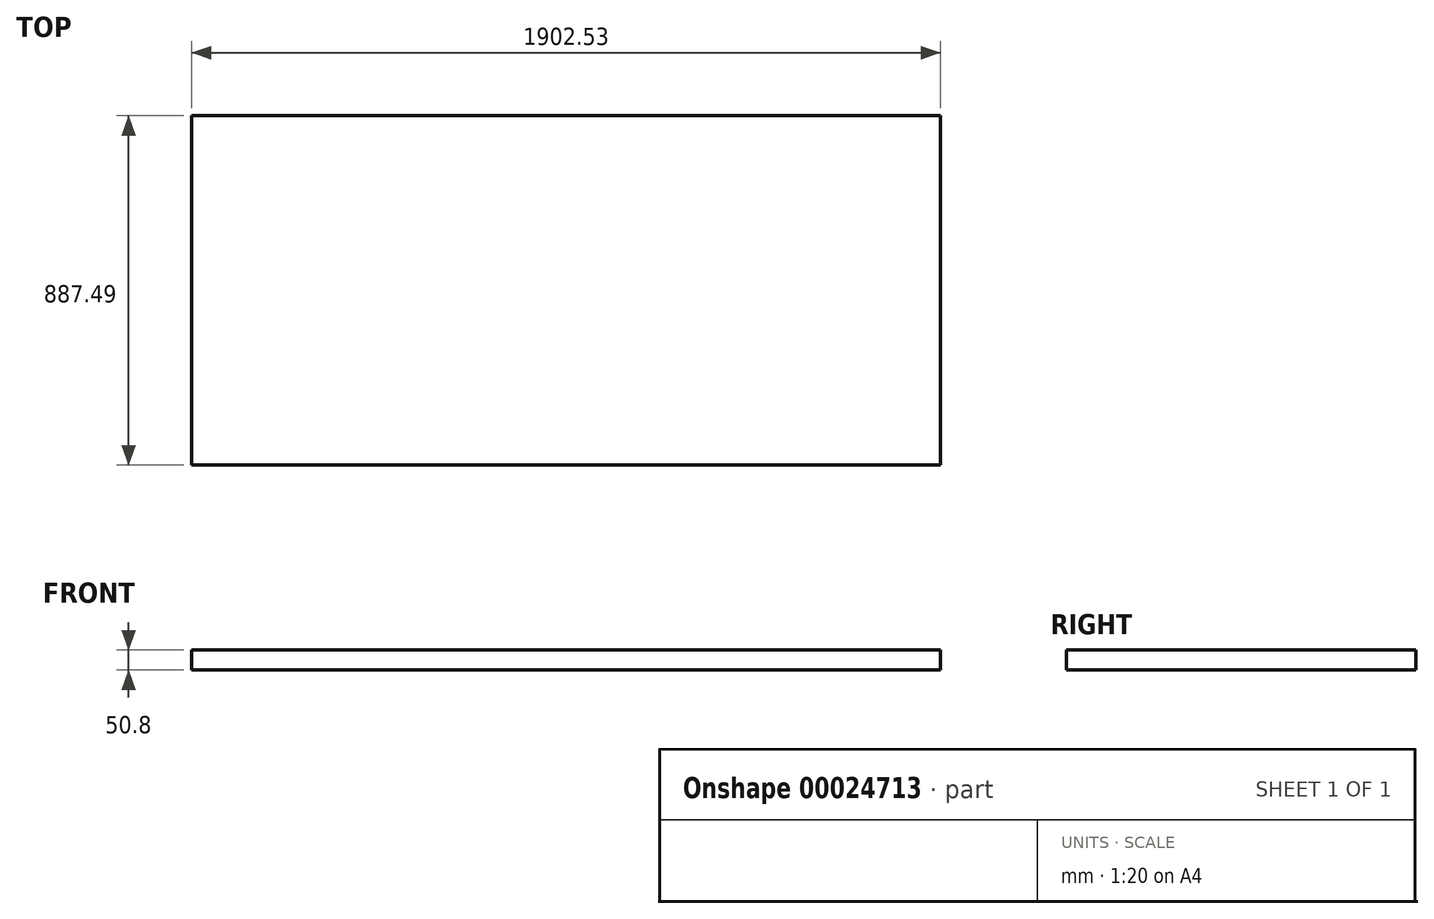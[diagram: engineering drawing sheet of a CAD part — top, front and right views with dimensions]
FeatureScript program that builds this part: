
annotation { "Feature Type Name" : "Feature", "Feature Type Description" : "" }
export const myFeature = defineFeature(function(context is Context, id is Id, definition is map)
    precondition{}
    {
        {
            var Q0;
            Q0=qCreatedBy(makeId("Top.planeOp"),FACE);
            var sketch = newSketch(context, id + "F0", { "sketchPlane" : qUnion([Q0])});
            skLineSegment(sketch, "E0.bottom", {"start": v(-989.78, 461.12) * mm, "end": v(912.75, 461.12) * mm});
            skLineSegment(sketch, "E0.top", {"start": v(-989.78, -426.37) * mm, "end": v(912.75, -426.37) * mm});
            skLineSegment(sketch, "E0.left", {"start": v(-989.78, 461.12) * mm, "end": v(-989.78, -426.37) * mm});
            skLineSegment(sketch, "E0.right", {"start": v(912.75, 461.12) * mm, "end": v(912.75, -426.37) * mm});
            skSolve(sketch);
        }
        {
            var Q0;
            Q0=makeQuery(id+"F0.imprint","IMPRINT",FACE,{"disambiguationData":[TD([[makeQuery(id+"F0.imprint","IMPRINT",EDGE,{"derivedFrom":sQuery(id+"F0.wireOp",EDGE,"E0.bottom")}),-1.0]])]});
            extrude(context, id + "F1", {"entities" : qUnion([Q0]), "depth" : 50.8 * mm});
        }
    });
